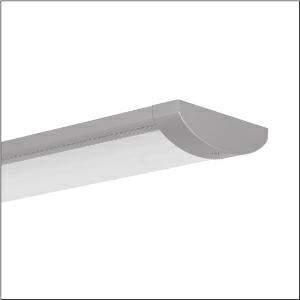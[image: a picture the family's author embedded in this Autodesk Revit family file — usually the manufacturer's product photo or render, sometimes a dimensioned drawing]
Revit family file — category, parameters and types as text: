
# Revit family: tv_20_5xa86172n0a
name_source: partatom
category: Lighting Fixtures
units: mm (PartAtom-declared; Revit-internal decimal feet)

## family parameters
Cut with Voids When Loaded = No
Host = Face
Light Source = No
Part Type = Normal
Room Calculation Point = No
Round Connector Dimension = Use Diameter
Shared = No

## types (1)
- TV 20 (1 x LED 4000K / CRI = 80 (unbekannt), 2130 lm, 4000K)
    Apparent Load = 21 VA
    CIE Flux Codes = 48 78 95 99 100
    Color Rendering = 80
    Color Temperature = 4000K
    Default Elevation = 1800 mm
    Description = TV 20, vandal-proof luminaire, primary light control with specular reflector, of aluminium, matt, primary optical cover: enclosure, of PC, frosted, light emission: direct distribution, primary light characteristic: symmetric, installation type: surface-mounted, LED, rated luminous flux: 2.130lm, luminous efficacy: 101lm/W, light colour: 840, colour temperature: 4000K, control gear: ECG, mains connection: 230V, AC, 50Hz, rated input power: 21W, luminaire housing, of aluminium, coated, Siteco® metallic grey (DB 702S), with wall and ceiling fixing element, length: 705mm, width: 260mm, height: 70mm, protection rating (complete): IP65, insulation class (complete): insulation class I (protective earthing), certification: CE, protection symbol: F, impact resistance: 2x IK10, standard: EN 60598, packaging unit: 1 piece
    Height = 70 mm
    Lamp = 1 x LED 4000K / CRI >= 80 (unbekannt)
    Lamp Light Flux = 2130 lm
    Lamp count = 1
    Length = 705 mm
    Luminous efficacy = 101 lm/W
    Manufacturer = Siteco
    ModVariant = No
    Model = 5XA86172N0A
    Mounting Place = Ceiling
    Mounting Type = Surface mounted
    Number of Poles = 1
    OnlyDefault = Yes
    Power Factor = 1
    Product Name = TV 20
    Product group = vandal-proof luminaire
    ProductGroupID = 307
    Protection Class = Protection class I
    Protection Degree = IP 65
    RLX_Detail_Level = 1
    RLX_Emergency_Light_Flux = 0 lm
    RLX_Emergency_Type = 0
    RLX_Emergency_Type_DB = No
    RlxData = <blob elided: 34109 chars, md5=6b4d6f1f>
    Socket = socket
    Standby Power = 0 W
    System Light Flux = 2130 lm
    System Power = 21 W
    Type Comments = Product without accessories
    Type Image = l_1004809.jpg
    URL = http://relux.com
    VarID = ---
    Voltage = 0 V
    Weight = 0.00 kg
    Width = 260 mm

## geometry (parser evidence)
native form markers: Blend x4, Sweep x10
no freeform markers — native parametric forms only
